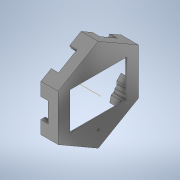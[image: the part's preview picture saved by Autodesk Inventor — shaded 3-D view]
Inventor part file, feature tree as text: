
AUTODESK INVENTOR PART (.ipt)
format: ipt  version: 2020 (Build 240168000, 168)  size: 790,528 bytes
history: native  units: mm
features: extrude x7, sketch x3, pattern_circular x1, chamfer x1, fillet x1, hole x1
ambient origin geometry x8: Origin, YZ Plane, XZ Plane, XY Plane, X Axis, Y Axis, Z Axis, Center Point
bodies: Body1 (feature_tree)
feature tree (14):
  sketch  "Sketch6"  dims[d44=97.0mm d72=6.5mm]
  extrude  "Fronte"  Depth=6.5mm
  extrude  "Esterno"  Depth=1.0mm TaperAngle=0.0deg
  extrude  "Strip"  Depth=6.5mm
  extrude  "Passacavi"  Depth=30.0mm
  extrude  "ScavoStrip"  Depth=2.0mm
  extrude  "ScreenDist0.8"  Depth=2.0mm
  extrude  "SupportoViti"  Depth=2.0mm
  pattern_circular  "RipetizioneSupports"  [2 undecoded]
  chamfer  "Smusso interno"  Distance=2.5mm
  fillet  "RaccordoSupports"  Radius=26.0mm
  hole  "ForoPulsante"  [1 undecoded]
  sketch  "Sketch7"  dims[d77=140.0mm d85=1.0mm d86=0.0mm]
  sketch  "Sketch9"  dims[d87=15.0mm d88=6.5mm d89=30.0mm d91=2.0mm d92=2.0mm d95=1.25mm d96=26.0mm d97=2.5mm d98=26.0mm d99=135.0deg d100=0.0mm d101=25.0mm d102=0.0mm d103=10.0mm d104=0.0mm d105=11.0mm d106=0.0mm d107=5.0mm d108=0.0mm d111=0.8mm d112=0.0mm d114=1.7mm d115=23.0mm d116=0.0mm d117=3.0mm d118=60.0mm d119=360.0deg d121=3.0mm d123=6.0mm d124=85.8mm d125=1.0mm d126=2.0mm d127=45.0deg d128=1.0mm d132=20.0mm d133=18.0mm d135=3.0mm d136=6.0mm d137=7.0mm d138=2.0mm d139=90.0deg d140=8.0mm d141=20.594885mm]
note: 3 required parameter values undecoded (feature->parameter linkage not recoverable at this tier; creation-order binding heuristic only, values carry confidence <= 0.55)
